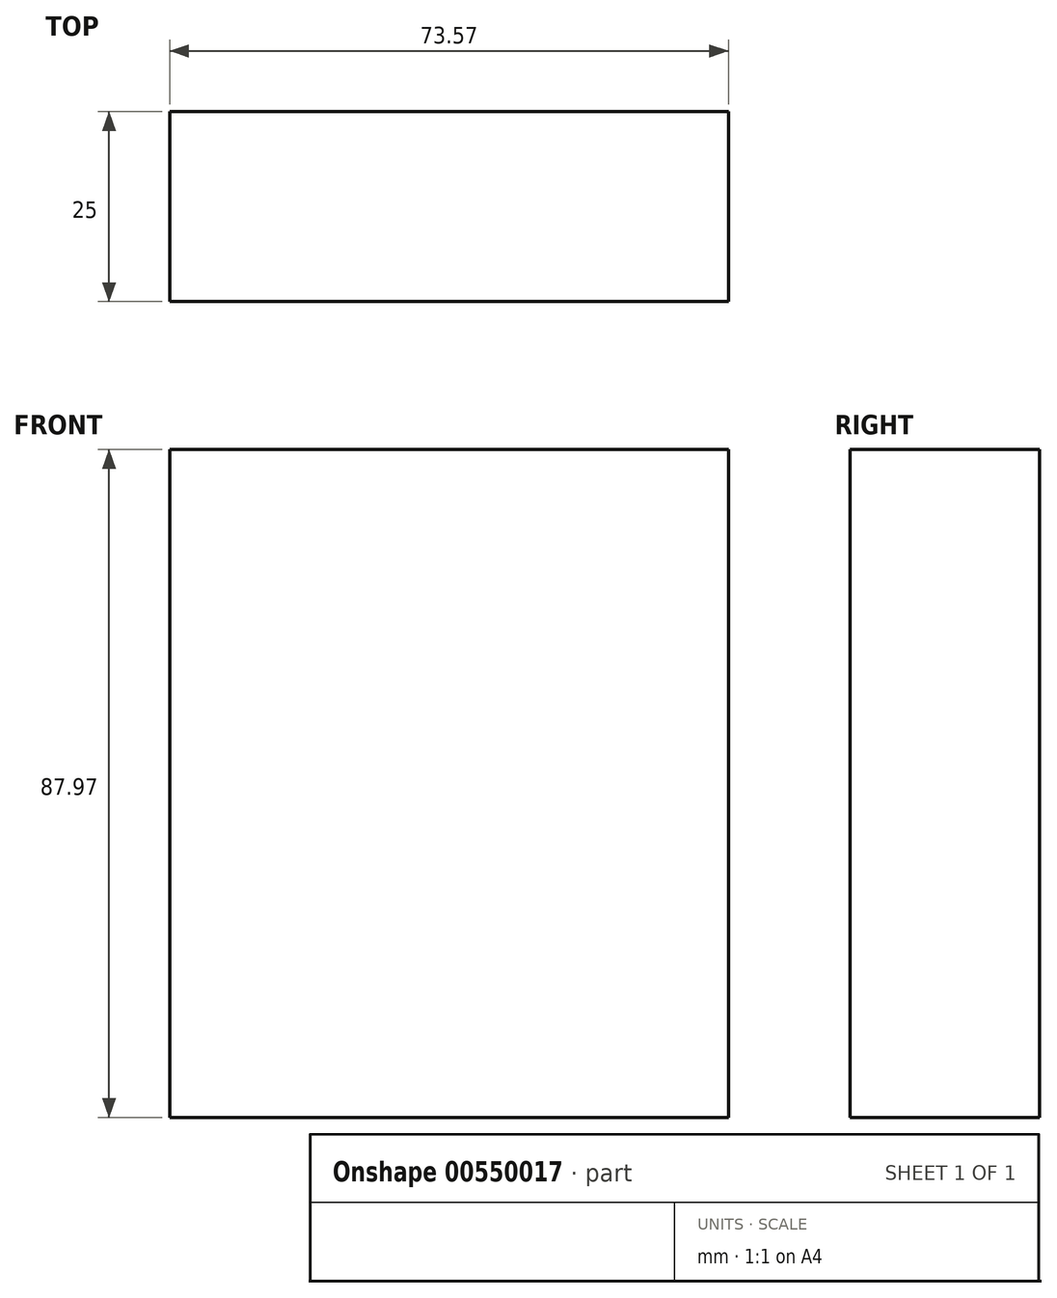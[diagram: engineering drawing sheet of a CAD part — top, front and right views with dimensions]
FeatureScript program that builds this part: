
annotation { "Feature Type Name" : "Feature", "Feature Type Description" : "" }
export const myFeature = defineFeature(function(context is Context, id is Id, definition is map)
    precondition{}
    {
        {
            var Q0;
            Q0=qCreatedBy(makeId("Front.planeOp"),FACE);
            var sketch = newSketch(context, id + "F0", { "sketchPlane" : qUnion([Q0])});
            skLineSegment(sketch, "E0.bottom", {"start": v(-31.08, 20.4) * mm, "end": v(42.49, 20.4) * mm});
            skLineSegment(sketch, "E0.top", {"start": v(-31.08, -67.57) * mm, "end": v(42.49, -67.57) * mm});
            skLineSegment(sketch, "E0.left", {"start": v(-31.08, 20.4) * mm, "end": v(-31.08, -67.57) * mm});
            skLineSegment(sketch, "E0.right", {"start": v(42.49, 20.4) * mm, "end": v(42.49, -67.57) * mm});
            skSolve(sketch);
        }
        {
            var Q0;
            Q0 = qSketchRegion(id + "F0", true);
            extrude(context, id + "F1", {"entities" : qUnion([Q0]), "depth" : 25 * mm, "offsetDistance" : 25 * mm});
        }
    });
